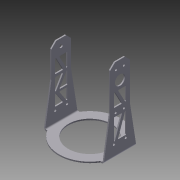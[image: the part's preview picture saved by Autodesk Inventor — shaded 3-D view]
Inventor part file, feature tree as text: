
AUTODESK INVENTOR PART (.ipt)
format: ipt  version: 2011 (Build 150239000, 239)  size: 236,544 bytes
history: native  units: mm
features: imported_body x1, other x1, plane x1
ambient origin geometry x8: Origin, YZ Plane, XZ Plane, XY Plane, X Axis, Y Axis, Z Axis, Center Point
bodies: Solid1 (feature_tree)
feature tree (3):
  imported_body  "Base1"
  other  "Work Axis1"
  plane  "Work Plane1"
